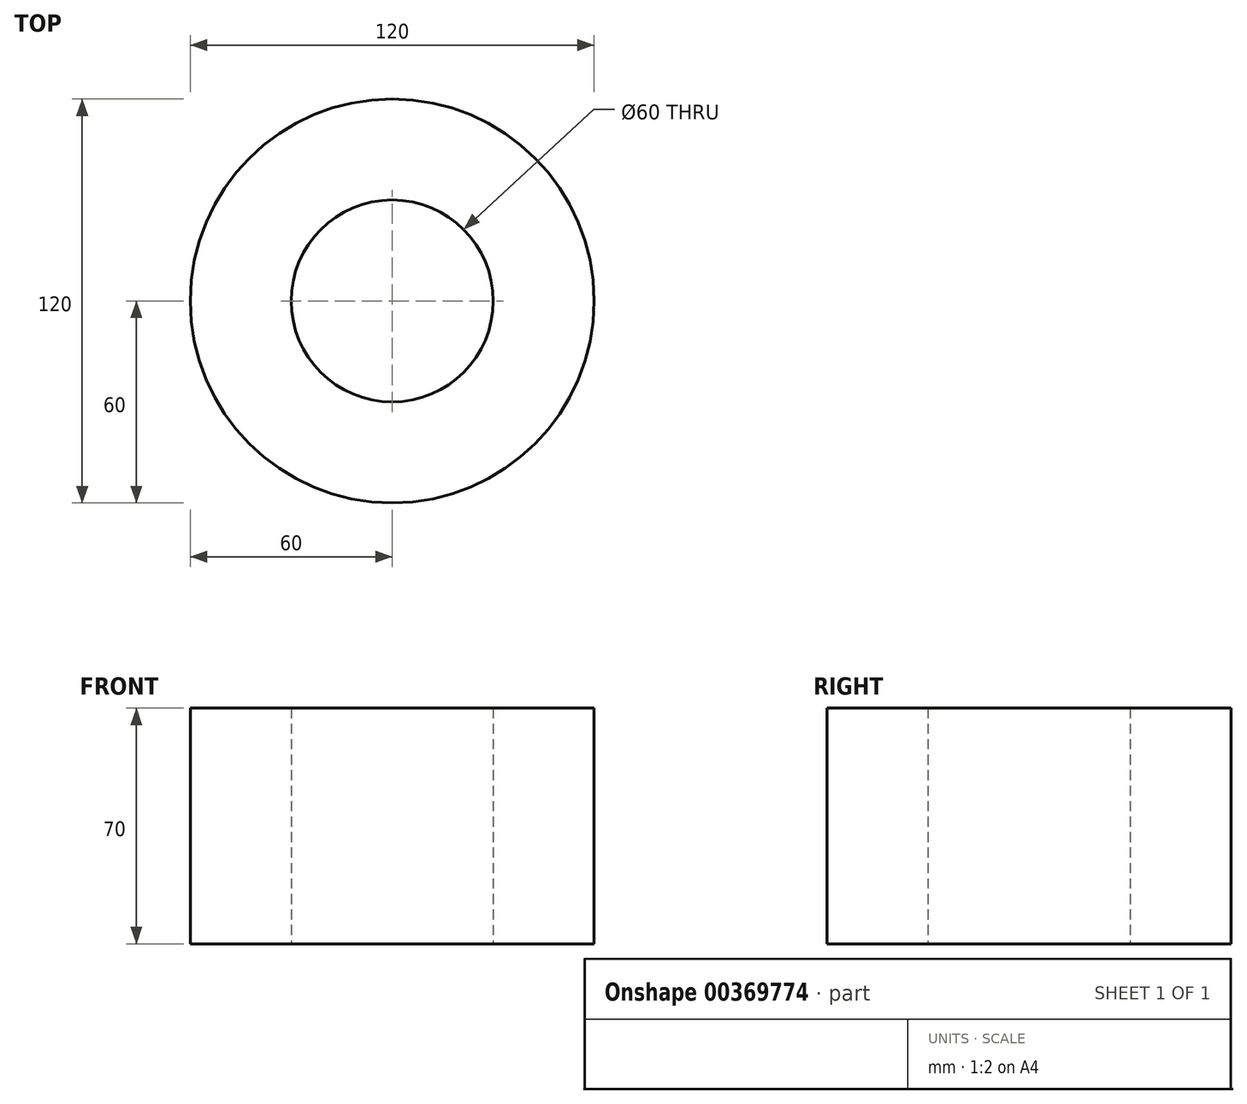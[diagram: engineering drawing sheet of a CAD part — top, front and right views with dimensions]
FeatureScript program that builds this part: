
annotation { "Feature Type Name" : "Feature", "Feature Type Description" : "" }
export const myFeature = defineFeature(function(context is Context, id is Id, definition is map)
    precondition{}
    {
        {
            var Q0;
            Q0=qCreatedBy(makeId("Top.planeOp"),FACE);
            var sketch = newSketch(context, id + "F0", { "sketchPlane" : qUnion([Q0])});
            skCircle(sketch, "E0", {"center": v(0, 0) * mm, "radius": 30 * mm});
            skCircle(sketch, "E1", {"center": v(0, 0) * mm, "radius": 60 * mm});
            skSolve(sketch);
        }
        {
            var Q0;
            Q0 = qSketchRegion(id + "F0", true);
            var Q1;
            Q1 = qConstructionFilter(qBodyType(qCreatedBy(id + "F0" ,EDGE), BodyType.WIRE), ConstructionObject.NO);
            extrude(context, id + "F1", {"entities" : qUnion([Q0]), "surfaceEntities" : qUnion([Q1]), "depth" : 70 * mm, "offsetDistance" : 25 * mm});
        }
    });
